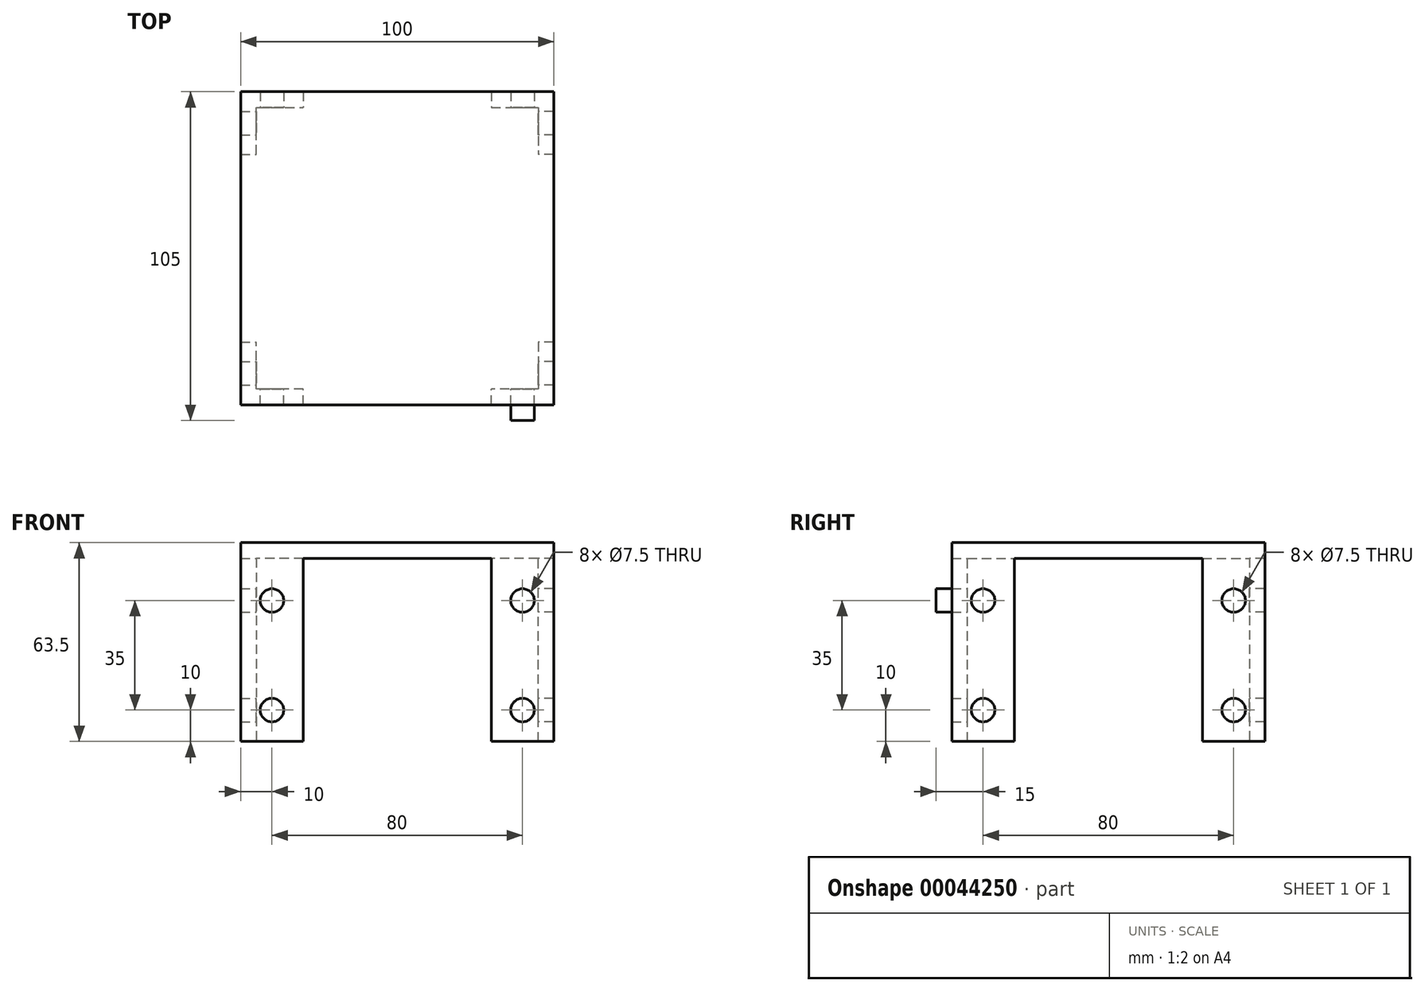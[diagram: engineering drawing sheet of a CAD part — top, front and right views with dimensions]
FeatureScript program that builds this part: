
annotation { "Feature Type Name" : "Feature", "Feature Type Description" : "" }
export const myFeature = defineFeature(function(context is Context, id is Id, definition is map)
    precondition{}
    {
        {
            var Q0;
            Q0=qCreatedBy(makeId("Front.planeOp"),FACE);
            var sketch = newSketch(context, id + "F0", { "sketchPlane" : qUnion([Q0])});
            skLineSegment(sketch, "E0", {"start": v(-50, 0) * mm, "end": v(-50, 58.5) * mm});
            skLineSegment(sketch, "E1", {"start": v(-50, 63.5) * mm, "end": v(50, 63.5) * mm});
            skCircle(sketch, "E2", {"center": v(40, 10) * mm, "radius": 3.75 * mm});
            skPoint(sketch, "E2.centerSnap0", {"position": v(40, 0) * mm});
            skCircle(sketch, "E3", {"center": v(40, 45) * mm, "radius": 3.75 * mm});
            skCircle(sketch, "E4", {"center": v(-40, 10) * mm, "radius": 3.75 * mm});
            skCircle(sketch, "E5", {"center": v(-40, 45) * mm, "radius": 3.75 * mm});
            skLineSegment(sketch, "E6", {"start": v(40, 0) * mm, "end": v(50, 0) * mm});
            skLineSegment(sketch, "E7", {"start": v(40, 0) * mm, "end": v(30, 0) * mm});
            skLineSegment(sketch, "E8", {"start": v(30, 0) * mm, "end": v(30, 58.5) * mm});
            skLineSegment(sketch, "E9", {"start": v(50, 58.5) * mm, "end": v(-30, 58.5) * mm});
            skLineSegment(sketch, "E10", {"start": v(-30, 58.5) * mm, "end": v(-30, 0) * mm});
            skLineSegment(sketch, "E11", {"start": v(-30, 0) * mm, "end": v(-50, 0) * mm});
            skLineSegment(sketch, "E12", {"start": v(-30, 58.5) * mm, "end": v(-50, 58.5) * mm});
            skLineSegment(sketch, "E13", {"start": v(50, 58.5) * mm, "end": v(50, 0) * mm});
            skLineSegment(sketch, "E14", {"start": v(-50, 58.5) * mm, "end": v(-50, 63.5) * mm});
            skLineSegment(sketch, "E15", {"start": v(50, 63.5) * mm, "end": v(50, 58.5) * mm});
            skPoint(sketch, "E16", {"position": v(0, 63.5) * mm});
            skLineSegment(sketch, "E17", {"start": v(0, 63.5) * mm, "end": v(0, 0) * mm, "construction": true});
            skSolve(sketch);
        }
        {
            var Q0;
            Q0=makeQuery(id+"F0.imprint","IMPRINT",FACE,{"disambiguationData":[TD([[makeQuery(id+"F0.imprint","IMPRINT",EDGE,{"derivedFrom":sQuery(id+"F0.wireOp",EDGE,"E0")}),-1.0]])]});
            var Q1;
            Q1=makeQuery(id+"F0.imprint","IMPRINT",FACE,{"disambiguationData":[TD([[makeQuery(id+"F0.imprint","IMPRINT",EDGE,{"derivedFrom":sQuery(id+"F0.wireOp",EDGE,"E2")}),-1.0]])]});
            var Q2;
            Q2=makeQuery(id+"F0.imprint","IMPRINT",FACE,{"disambiguationData":[TD([[makeQuery(id+"F0.imprint","IMPRINT",EDGE,{"derivedFrom":sQuery(id+"F0.wireOp",EDGE,"E1")}),-1.0]])]});
            extrude(context, id + "F1", {"entities" : qUnion([Q0, Q1, Q2]), "depth" : 50 * mm, "offsetDistance" : 25 * mm, "hasSecondDirection" : true, "secondDirectionOppositeDirection" : false, "secondDirectionDepth" : 45 * mm});
        }
        {
            var Q0;
            Q0=makeQuery(id+"F0.imprint","IMPRINT",FACE,{"disambiguationData":[TD([[makeQuery(id+"F0.imprint","IMPRINT",EDGE,{"derivedFrom":sQuery(id+"F0.wireOp",EDGE,"E1")}),-1.0]])]});
            extrude(context, id + "F2", {"entities" : qUnion([Q0]), "operationType" : NewBodyOperationType.ADD, "endBound" : BoundingType.UP_TO_NEXT, "depth" : 25 * mm, "offsetDistance" : 25 * mm});
        }
        {
            var Q0;
            Q0=makeQuery(id+"F1.opExtrude","SWEPT_BODY",BODY,{"disambiguationData":[OSD([sQuery(id+"F0.wireOp",EDGE,"E0"),sQuery(id+"F0.wireOp",EDGE,"E1"),sQuery(id+"F0.wireOp",EDGE,"E2"),sQuery(id+"F0.wireOp",EDGE,"E3"),sQuery(id+"F0.wireOp",EDGE,"E4"),sQuery(id+"F0.wireOp",EDGE,"E5"),sQuery(id+"F0.wireOp",EDGE,"E6"),sQuery(id+"F0.wireOp",EDGE,"E7"),sQuery(id+"F0.wireOp",EDGE,"E8"),sQuery(id+"F0.wireOp",EDGE,"E9"),sQuery(id+"F0.wireOp",EDGE,"E10"),sQuery(id+"F0.wireOp",EDGE,"E11"),sQuery(id+"F0.wireOp",EDGE,"E13"),sQuery(id+"F0.wireOp",EDGE,"E14"),sQuery(id+"F0.wireOp",EDGE,"E15")])]});
            var Q1;
            Q1=sQuery(id+"F0.wireOp",EDGE,"E17");
            circularPattern(context, id + "F3", {"operationType" : NewBodyOperationType.ADD, "entities" : qUnion([Q0]), "axis" : qUnion([Q1]), "angle" : 360 * degree, "instanceCount" : 4, "equalSpace" : true});
        }
        {
            var Q0;
            {var subQ0=sQuery(id+"F0.wireOp",EDGE,"E7");var subQ1=sQuery(id+"F0.wireOp",EDGE,"E6");var subQ2=sQuery(id+"F0.wireOp",EDGE,"E15");var subQ3=sQuery(id+"F0.wireOp",EDGE,"E3");var subQ4=sQuery(id+"F0.wireOp",EDGE,"E8");var subQ5=sQuery(id+"F0.wireOp",EDGE,"E2");var subQ6=sQuery(id+"F0.wireOp",EDGE,"E9");var subQ7=sQuery(id+"F0.wireOp",EDGE,"E13");Q0=makeQuery(id+"F2.boolean.opBoolean","SPLIT",FACE,{"disambiguationData":[TD([makeQuery(id+"F1.opExtrude","SWEPT_FACE",FACE,{"disambiguationData":[OSD([subQ5])]})])],"derivedFrom":makeQuery(id+"F1.opExtrude","CAP_FACE",FACE,{"disambiguationData":[OSD([sQuery(id+"F0.wireOp",EDGE,"E0"),sQuery(id+"F0.wireOp",EDGE,"E1"),subQ5,subQ3,sQuery(id+"F0.wireOp",EDGE,"E4"),sQuery(id+"F0.wireOp",EDGE,"E5"),subQ1,subQ0,subQ4,subQ6,sQuery(id+"F0.wireOp",EDGE,"E10"),sQuery(id+"F0.wireOp",EDGE,"E11"),subQ7,sQuery(id+"F0.wireOp",EDGE,"E14"),subQ2])],"isStart":true})});}
            var sketch = newSketch(context, id + "F4", { "sketchPlane" : qUnion([Q0])});
            skSolve(sketch);
        }
        {
            var Q0;
            Q0=makeQuery(id+"F4.imprint","IMPRINT",FACE,{"disambiguationData":[TD([[makeQuery(id+"F4.imprint","IMPRINT",EDGE,{"derivedFrom":makeQuery(id+"F1.opExtrude","CAP_EDGE",EDGE,{"disambiguationData":[OSD([sQuery(id+"F0.wireOp",EDGE,"E3")])],"isStart":true})}),-1.0]])]});
            extrude(context, id + "F5", {"entities" : qUnion([Q0]), "oppositeDirection" : true, "depth" : 10 * mm, "offsetDistance" : 25 * mm});
        }
        {
            var Q0;
            Q0=qCreatedBy(makeId("Front.planeOp"),FACE);
            var sketch = newSketch(context, id + "F6", { "sketchPlane" : qUnion([Q0])});
            skPoint(sketch, "E18.0", {"position": v(50, 63.5) * mm});
            skPoint(sketch, "E19.0", {"position": v(50, 0) * mm});
            skLineSegment(sketch, "E20", {"start": v(50, 63.5) * mm, "end": v(174.43, 0) * mm, "construction": true});
            skLineSegment(sketch, "E21", {"start": v(174.43, 0) * mm, "end": v(50, 0) * mm, "construction": true});
            skLineSegment(sketch, "E22", {"start": v(50, 63.5) * mm, "end": v(50, 0) * mm, "construction": true});
            skSolve(sketch);
        }
        {
            var Q0;
            {var subQ0=sQuery(id+"F0.wireOp",EDGE,"E15");var subQ1=sQuery(id+"F0.wireOp",EDGE,"E14");var subQ2=sQuery(id+"F0.wireOp",EDGE,"E13");var subQ3=sQuery(id+"F0.wireOp",EDGE,"E0");Q0=makeQuery(id+"F3.boolean.opBoolean","MERGE",FACE,{"derivedFrom":[makeQuery(id+"F2.boolean.opBoolean","MERGE",FACE,{"derivedFrom":[makeQuery(id+"F1.opExtrude","SWEPT_FACE",FACE,{"disambiguationData":[OSD([subQ2,subQ0])]}),makeQuery(id+"F2.opExtrude","SWEPT_FACE",FACE,{"disambiguationData":[OSD([subQ0])]})]}),makeQuery(id+"F3.opPattern","COPY",FACE,{"derivedFrom":makeQuery(id+"F2.boolean.opBoolean","MERGE",FACE,{"derivedFrom":[makeQuery(id+"F1.opExtrude","SWEPT_FACE",FACE,{"disambiguationData":[OSD([subQ3,subQ1])]}),makeQuery(id+"F2.opExtrude","SWEPT_FACE",FACE,{"disambiguationData":[OSD([subQ1])]})]}),"instanceName":"2"}),makeQuery(id+"F3.opPattern","COPY",FACE,{"derivedFrom":makeQuery(id+"F1.opExtrude","CAP_FACE",FACE,{"disambiguationData":[OSD([subQ3,sQuery(id+"F0.wireOp",EDGE,"E1"),sQuery(id+"F0.wireOp",EDGE,"E2"),sQuery(id+"F0.wireOp",EDGE,"E3"),sQuery(id+"F0.wireOp",EDGE,"E4"),sQuery(id+"F0.wireOp",EDGE,"E5"),sQuery(id+"F0.wireOp",EDGE,"E6"),sQuery(id+"F0.wireOp",EDGE,"E7"),sQuery(id+"F0.wireOp",EDGE,"E8"),sQuery(id+"F0.wireOp",EDGE,"E9"),sQuery(id+"F0.wireOp",EDGE,"E10"),sQuery(id+"F0.wireOp",EDGE,"E11"),subQ2,subQ1,subQ0])],"isStart":false}),"instanceName":"3"})]});}
            cPlane(context, id + "F7", {"entities" : qUnion([Q0]), "cplaneType" : CPlaneType.OFFSET, "offset" : 0 * mm, "width" : 150 * mm, "height" : 150 * mm});
        }
    });
